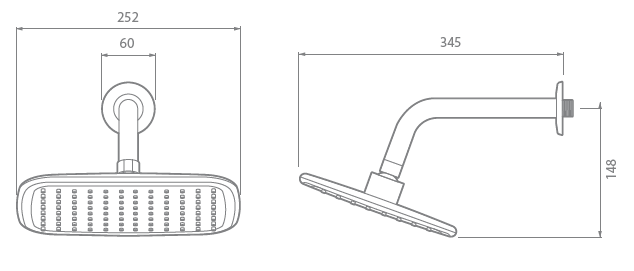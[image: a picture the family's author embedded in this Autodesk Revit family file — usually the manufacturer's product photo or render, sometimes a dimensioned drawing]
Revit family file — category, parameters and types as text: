
# Revit family: TH4115551_Ducha Monocontrol Thames PRO SSB
name_source: partatom
category: Plumbing Fixtures
units: mm (PartAtom-declared; Revit-internal decimal feet)

## family parameters
Always vertical = Yes
Cut with Voids When Loaded = No
Host = Wall
OmniClass Number = 23.31.15.11
OmniClass Title = Bath Shower Units
Part Type = Normal
Room Calculation Point = No
Round Connector Dimension = Use Diameter
Shared = No

## types (1)
- Type 1
    Acabado = Cromado
    Alto = 14.8 cm
    Altura ducha = 1800 mm  [stored 5.90551 ft]
    Altura mezclador = 700 mm  [stored 2.29659 ft]
    Ancho = 25.2 cm
    Capacidad de flujo = 9.30 l/m máximo a 80 psi
    Colección = Regaderas y Teleduchas 2019
    Consumo de agua = 9.3 lt
    Creado por = IDD
    Description = Con la ducha Thames tienes la oportunidad de disfrutar de la tecnología de ahorro de agua que minimiza el derroche, ofreciendo un mayor rendimiento sin sacrificar el confort en la ducha. Ahora tus baños serán toda una experiencia.
    Dimensión de la regadera = 25.20
    Fecha de creación = 21/07/2020
    Forma = Rectangular
    Garantía = 30 años en estructura
    Garantías de otros componentes = 2 años en acabados
    Largo = 34.5 cm
    Longitud del brazo = 34.5
    Línea = Thames
    Manufacturer = Corona
    Material = Corona_Cromado
    Materiales = Polímero de alta ingeniería Metal
    Model = Ducha Monocontrol Thames PRO SSB
    Peso neto = 1.200 g. - 2,64 lb
    Productos compatibles = Cuerpo, regadera, brazo de la regadera y escudo, manija
    Rango de presión de agua = Entre 20 y 125 psi
    Resistencia = Resistente a la corrosión pelado y decoloración por agua
    Sistema de accionamiento = Palanca
    Temperatura de uso = Entre 5˚C y 71˚C
    Tipo de chorro = Tipo lluvia
    Tipo de grifería = Monocontrol
    Tipo de manija/accionamiento = Palanca
    Tipo de regadera = Sencilla Regadera con brazo
    Tipo mezclador = Monocontrol
    URL = https://corona.co
    Uso = Residencial

note: [stored X ft] marks values corroborated as IEEE doubles in the binary element streams (Revit-internal decimal feet)

## geometry (parser evidence)
native form markers: Sweep x10
no freeform markers — native parametric forms only
